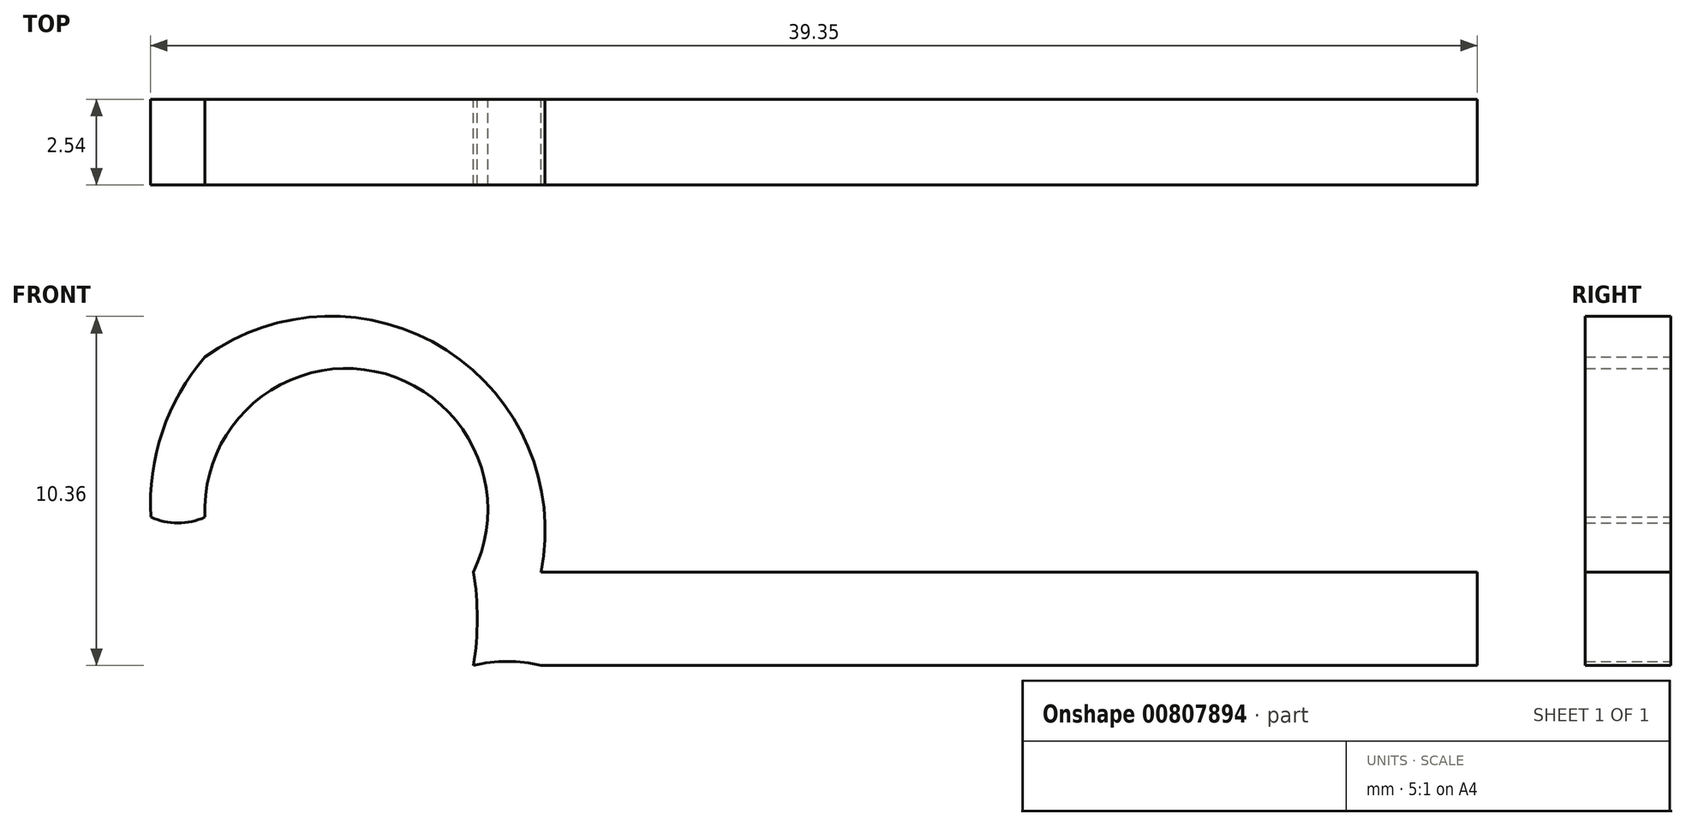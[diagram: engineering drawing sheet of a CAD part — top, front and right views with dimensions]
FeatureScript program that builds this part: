
annotation { "Feature Type Name" : "Feature", "Feature Type Description" : "" }
export const myFeature = defineFeature(function(context is Context, id is Id, definition is map)
    precondition{}
    {
        {
            var Q0;
            Q0=qCreatedBy(makeId("Front.planeOp"),FACE);
            var sketch = newSketch(context, id + "F0", { "sketchPlane" : qUnion([Q0])});
            skLineSegment(sketch, "E0.bottom", {"start": v(27.77, 0) * mm, "end": v(0, 0) * mm});
            skLineSegment(sketch, "E0.top", {"start": v(27.77, 2.77) * mm, "end": v(0, 2.77) * mm});
            skLineSegment(sketch, "E0.left", {"start": v(27.77, 0) * mm, "end": v(27.77, 2.77) * mm});
            skLineSegment(sketch, "E0.right", {"start": v(0, 0) * mm, "end": v(0, 2.77) * mm});
            skArc(sketch, "E1", {"start": v(0, 2.77) * mm, "mid": v(-2.8, 9.36) * mm, "end": v(-9.96, 9.15) * mm});
            skArc(sketch, "E2", {"start": v(-9.96, 9.15) * mm, "mid": v(-11.23, 6.93) * mm, "end": v(-11.57, 4.4) * mm});
            skArc(sketch, "E3", {"start": v(-11.57, 4.4) * mm, "mid": v(-10.77, 4.23) * mm, "end": v(-9.96, 4.4) * mm});
            skArc(sketch, "E4", {"start": v(-2, 2.77) * mm, "mid": v(-4.93, 8.73) * mm, "end": v(-9.96, 4.4) * mm});
            skArc(sketch, "E5", {"start": v(-2, 0) * mm, "mid": v(-1.89, 1.39) * mm, "end": v(-2, 2.77) * mm});
            skArc(sketch, "E6", {"start": v(0, 0) * mm, "mid": v(-1, 0.11) * mm, "end": v(-2, 0) * mm});
            skSolve(sketch);
        }
        {
            var Q0;
            Q0 = qSketchRegion(id + "F0", true);
            extrude(context, id + "F1", {"entities" : qUnion([Q0]), "depth" : 2.54 * mm, "offsetDistance" : 25.4 * mm});
        }
    });
